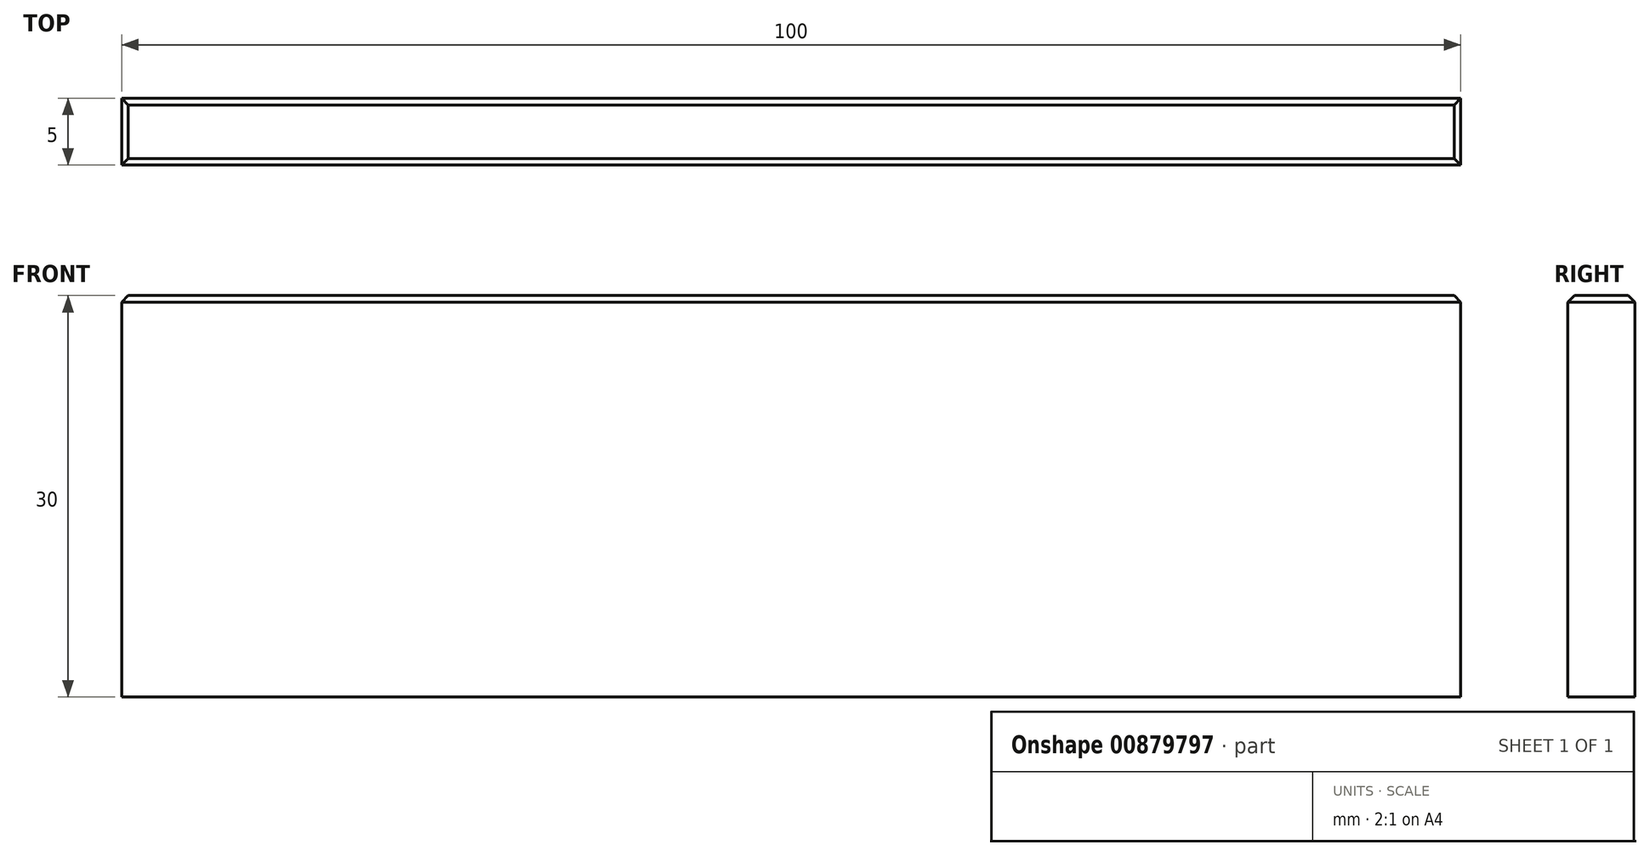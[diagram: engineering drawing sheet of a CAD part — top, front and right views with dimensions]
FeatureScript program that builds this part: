
annotation { "Feature Type Name" : "Feature", "Feature Type Description" : "" }
export const myFeature = defineFeature(function(context is Context, id is Id, definition is map)
    precondition{}
    {
        {
            var Q0;
            Q0=qCreatedBy(makeId("Front.planeOp"),FACE);
            var sketch = newSketch(context, id + "F0", { "sketchPlane" : qUnion([Q0])});
            skLineSegment(sketch, "E0.bottom", {"start": v(-50, 15) * mm, "end": v(50, 15) * mm});
            skLineSegment(sketch, "E0.top", {"start": v(-50, -15) * mm, "end": v(50, -15) * mm});
            skLineSegment(sketch, "E0.left", {"start": v(-50, 15) * mm, "end": v(-50, -15) * mm});
            skLineSegment(sketch, "E0.right", {"start": v(50, 15) * mm, "end": v(50, -15) * mm});
            skSolve(sketch);
        }
        {
            var Q0;
            Q0=makeQuery(id+"F0.imprint","IMPRINT",FACE,{"disambiguationData":[TD([[makeQuery(id+"F0.imprint","IMPRINT",EDGE,{"derivedFrom":sQuery(id+"F0.wireOp",EDGE,"E0.bottom")}),-1.0]])]});
            extrude(context, id + "F1", {"entities" : qUnion([Q0]), "depth" : 5 * mm, "offsetDistance" : 25 * mm, "symmetric" : true});
        }
        {
            var Q0;
            Q0=makeQuery(id+"F1.opExtrude","CAP_EDGE",EDGE,{"disambiguationData":[OSD([sQuery(id+"F0.wireOp",EDGE,"E0.bottom")])],"isStart":true});
            var Q1;
            Q1=makeQuery(id+"F1.opExtrude","CAP_EDGE",EDGE,{"disambiguationData":[OSD([sQuery(id+"F0.wireOp",EDGE,"E0.bottom")])],"isStart":false});
            var Q2;
            Q2=makeQuery(id+"F1.opExtrude","SWEPT_EDGE",EDGE,{"disambiguationData":[OSD([sQuery(id+"F0.wireOp",EDGE,"E0.bottom"),sQuery(id+"F0.wireOp",EDGE,"E0.left")])]});
            var Q3;
            Q3=makeQuery(id+"F1.opExtrude","SWEPT_EDGE",EDGE,{"disambiguationData":[OSD([sQuery(id+"F0.wireOp",EDGE,"E0.bottom"),sQuery(id+"F0.wireOp",EDGE,"E0.right")])]});
            chamfer(context, id + "F2", {"entities" : qUnion([Q0, Q1, Q2, Q3]), "width" : 0.5 * mm, "tangentPropagation" : true});
        }
    });
